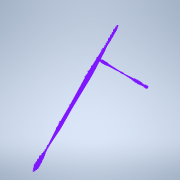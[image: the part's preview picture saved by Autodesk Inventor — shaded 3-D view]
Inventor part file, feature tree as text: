
AUTODESK INVENTOR PART (.ipt)
format: ipt  version: 2021 (Build 250183000, 183)  size: 976,896 bytes
history: native  units: in
note: dims shown in document units (in); Inventor stores cm internally (conversion verified against a paired STEP export)
features: sketch x4, other x1
ambient origin geometry x8: Origin, YZ Plane, XZ Plane, XY Plane, X Axis, Y Axis, Z Axis, Center Point
feature tree (5):
  other  "Repaired Geometry1"
  sketch  "Sketch4"
  sketch  "Sketch5"
  sketch  "Sketch6"
  sketch  "3D Sketch1"
